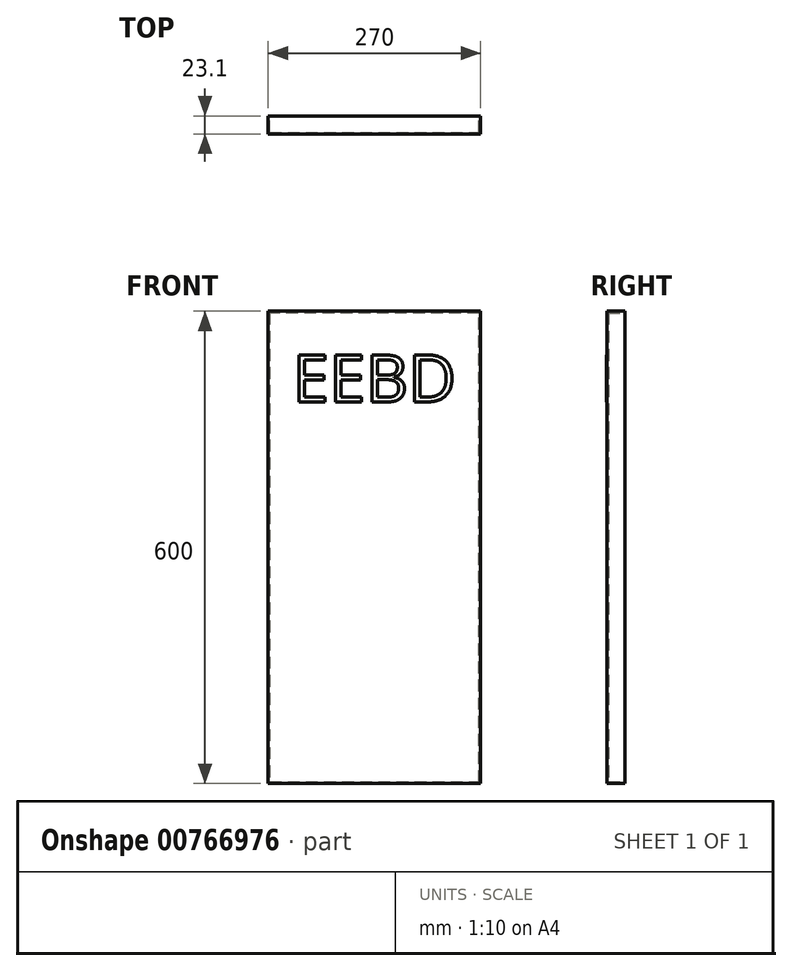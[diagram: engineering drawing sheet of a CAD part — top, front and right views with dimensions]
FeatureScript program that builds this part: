
annotation { "Feature Type Name" : "Feature", "Feature Type Description" : "" }
export const myFeature = defineFeature(function(context is Context, id is Id, definition is map)
    precondition{}
    {
        {
            var Q0;
            Q0=qCreatedBy(makeId("Front.planeOp"),FACE);
            var sketch = newSketch(context, id + "F0", { "sketchPlane" : qUnion([Q0])});
            skLineSegment(sketch, "E0", {"start": v(0, 0) * mm, "end": v(270, 0) * mm});
            skLineSegment(sketch, "E1", {"start": v(270, 0) * mm, "end": v(270, 600) * mm});
            skLineSegment(sketch, "E2", {"start": v(270, 600) * mm, "end": v(0, 600) * mm});
            skLineSegment(sketch, "E3", {"start": v(0, 600) * mm, "end": v(0, 0) * mm});
            skSolve(sketch);
        }
        {
            var Q0;
            Q0 = qSketchRegion(id + "F0", true);
            extrude(context, id + "F1", {"entities" : qUnion([Q0]), "depth" : 23 * mm, "offsetDistance" : 25 * mm});
        }
        {
            var Q0;
            Q0=makeQuery(id+"F1.opExtrude","CAP_FACE",FACE,{"disambiguationData":[OSD([sQuery(id+"F0.wireOp",EDGE,"E0"),sQuery(id+"F0.wireOp",EDGE,"E1"),sQuery(id+"F0.wireOp",EDGE,"E2"),sQuery(id+"F0.wireOp",EDGE,"E3")])],"isStart":true});
            shell(context, id + "F2", {"entities" : qUnion([Q0]), "thickness" : 2 * mm});
        }
        {
            var Q0;
            Q0=makeQuery(id+"F1.opExtrude","CAP_FACE",FACE,{"disambiguationData":[OSD([sQuery(id+"F0.wireOp",EDGE,"E0"),sQuery(id+"F0.wireOp",EDGE,"E1"),sQuery(id+"F0.wireOp",EDGE,"E2"),sQuery(id+"F0.wireOp",EDGE,"E3")])],"isStart":false});
            var sketch = newSketch(context, id + "F3", { "sketchPlane" : qUnion([Q0])});
            skText(sketch, "E4", { "text": "EEBD", "fontName": "OpenSans-Regular.ttf"});
            skPoint(sketch, "E5", {"position": v(135, 600) * mm});
            const initialGuessF3  = {"E4": [0.03113, 0.48487, 1, 0, 0.06]};
            skSetInitialGuess(sketch, initialGuessF3);
            skSolve(sketch);
        }
        {
            var Q0;
            Q0 = qSketchRegion(id + "F3", true);
            extrude(context, id + "F4", {"entities" : qUnion([Q0]), "operationType" : NewBodyOperationType.ADD, "depth" : 0.1 * mm, "offsetDistance" : 25 * mm});
        }
    });
